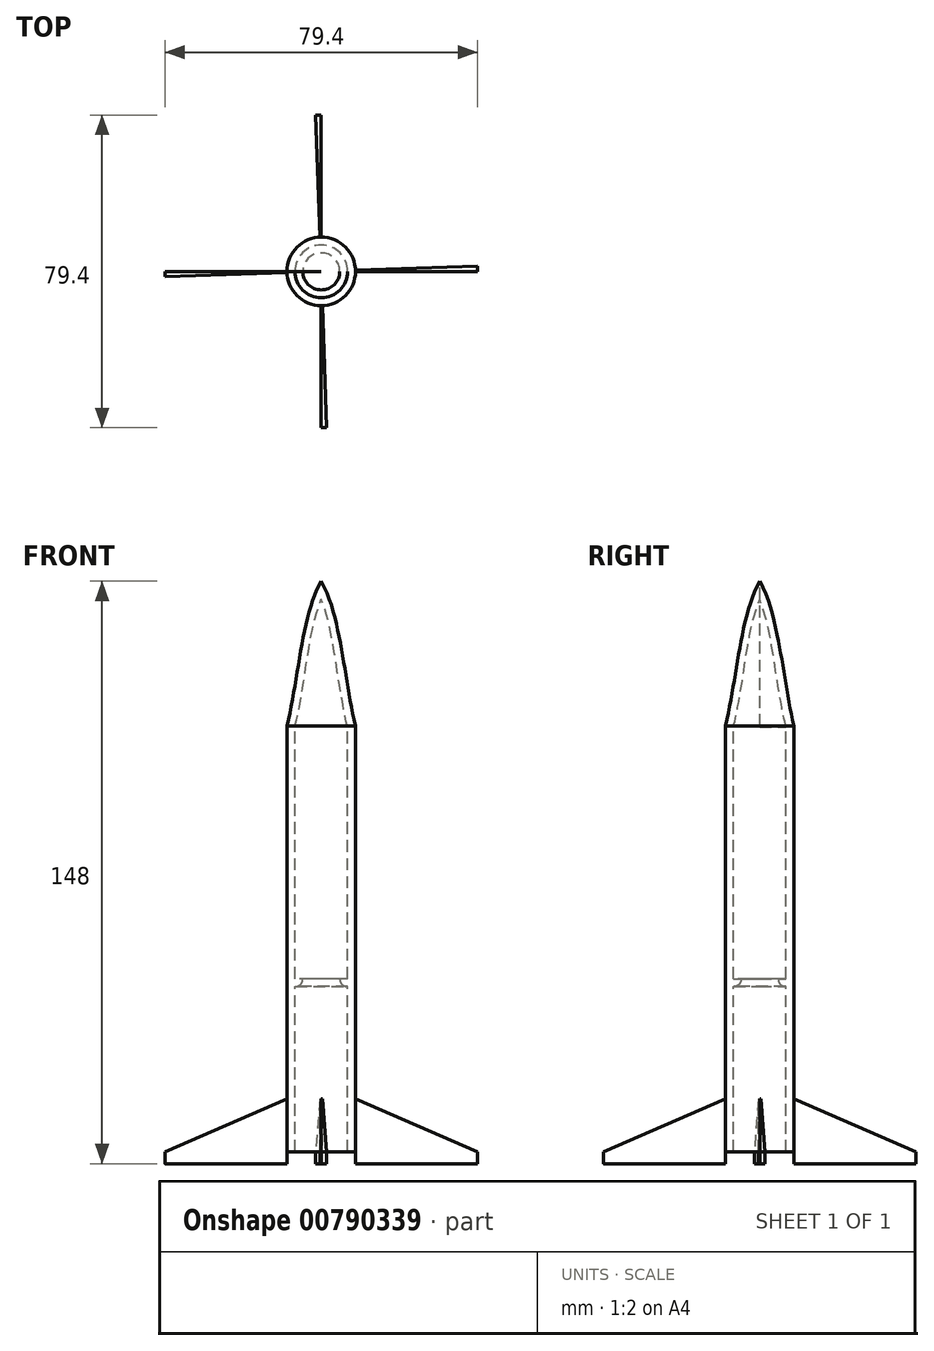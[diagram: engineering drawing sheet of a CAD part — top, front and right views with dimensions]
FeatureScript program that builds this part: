
annotation { "Feature Type Name" : "Feature", "Feature Type Description" : "" }
export const myFeature = defineFeature(function(context is Context, id is Id, definition is map)
    precondition{}
    {
        {
            var Q0;
            Q0=qCreatedBy(makeId("Front.planeOp"),FACE);
            var sketch = newSketch(context, id + "F0", { "sketchPlane" : qUnion([Q0])});
            skLineSegment(sketch, "E0", {"start": v(0, 145) * mm, "end": v(0, 143) * mm});
            skLineSegment(sketch, "E1", {"start": v(0, 143) * mm, "end": v(-13.5, 143) * mm, "construction": true});
            skLineSegment(sketch, "E2", {"start": v(-6.7, 108) * mm, "end": v(-6.7, 0) * mm});
            skLineSegment(sketch, "E3.1", {"start": v(-8.7, 108.2) * mm, "end": v(-8.7, 0) * mm});
            skLineSegment(sketch, "E4", {"start": v(-8.7, 0) * mm, "end": v(-6.7, 0) * mm});
            skLineSegment(sketch, "E5", {"start": v(-6.7, 0) * mm, "end": v(-6.7, 42) * mm});
            skLineSegment(sketch, "E6", {"start": v(-6.7, 42) * mm, "end": v(-4.7, 42) * mm});
            skLineSegment(sketch, "E7", {"start": v(-4.7, 42) * mm, "end": v(-4.7, 44) * mm});
            skLineSegment(sketch, "E8", {"start": v(-4.7, 44) * mm, "end": v(-6.7, 44) * mm});
            skLineSegment(sketch, "E9", {"start": v(0, 145) * mm, "end": v(0, 0) * mm});
            skLineSegment(sketch, "E10", {"start": v(-6.7, 108) * mm, "end": v(0, 108) * mm, "construction": true});
            skLineSegment(sketch, "E11", {"start": v(-8.7, 108.2) * mm, "end": v(0, 108) * mm, "construction": true});
            skLineSegment(sketch, "E12", {"start": v(0, 143) * mm, "end": v(0, 136.34) * mm, "construction": true});
            skFitSpline(sketch, "E13", {"points": [v(-8.7, 108.2) * mm, v(0, 145) * mm], "startDerivative": vector(8.7, 36.8) * mm, "endDerivative": vector(14.37, 24.57) * mm});
            skLineSegment(sketch, "E14", {"start": v(0, 145) * mm, "end": v(0, 136.34) * mm});
            skFitSpline(sketch, "E15.0", {"points": [v(-6.75, 107.75) * mm, v(-6, 110.89) * mm, v(-4.78, 117.6) * mm, v(-3.15, 127.92) * mm, v(-1.5, 135.77) * mm, v(0.2, 140.96) * mm, v(1.2, 143.08) * mm, v(1.73, 144) * mm]});
            skSolve(sketch);
        }
        {
            var Q0;
            {var subQ0=sQuery(id+"F0.wireOp",EDGE,"E3.1");Q0=makeQuery(id+"F0.imprint","IMPRINT",FACE,{"disambiguationData":[TD([[makeQuery(id+"F0.imprint","IMPRINT",EDGE,{"derivedFrom":subQ0}),1.0]])]});}
            var Q1;
            {var subQ0=sQuery(id+"F0.wireOp",EDGE,"E6");Q1=makeQuery(id+"F0.imprint","IMPRINT",FACE,{"disambiguationData":[TD([[makeQuery(id+"F0.imprint","IMPRINT",EDGE,{"derivedFrom":subQ0}),1.0]])]});}
            var Q2;
            {var subQ0=sQuery(id+"F0.wireOp",EDGE,"E9");var subQ1=sQuery(id+"F0.wireOp",EDGE,"E1");var subQ2=makeQuery(id+"F0.imprint","INTERSECT",VERTEX,{"derivedFrom":[subQ1,subQ0]});Q2=makeQuery(id+"F0.imprint","IMPRINT",FACE,{"disambiguationData":[TD([[makeQuery(id+"F0.imprint","IMPRINT",EDGE,{"disambiguationData":[TD([[subQ2,-1.0]])],"derivedFrom":subQ1}),-1.0]])]});}
            var Q3;
            Q3=sQuery(id+"F0.wireOp",EDGE,"E9");
            revolve(context, id + "F1", {"surfaceOperationType" : NewSurfaceOperationType.NEW, "entities" : qUnion([Q0, Q1, Q2]), "axis" : qUnion([Q3]), "revolveType" : RevolveType.FULL});
        }
        {
            var Q0;
            Q0=qCreatedBy(makeId("Right.planeOp"),FACE);
            var sketch = newSketch(context, id + "F2", { "sketchPlane" : qUnion([Q0])});
            skLineSegment(sketch, "E16", {"start": v(8.7, -3) * mm, "end": v(39.7, -3) * mm});
            skLineSegment(sketch, "E17", {"start": v(39.7, -3) * mm, "end": v(39.7, 0) * mm});
            skLineSegment(sketch, "E18", {"start": v(8.7, 0) * mm, "end": v(8.7, 13.5) * mm});
            skLineSegment(sketch, "E19", {"start": v(8.7, 13.5) * mm, "end": v(39.7, 0) * mm});
            skLineSegment(sketch, "E20", {"start": v(8.7, -3) * mm, "end": v(8.7, 0) * mm});
            skLineSegment(sketch, "E21", {"start": v(0, 0) * mm, "end": v(0, 51.2) * mm});
            skLineSegment(sketch, "E22", {"start": v(8.7, 0) * mm, "end": v(0, 0) * mm, "construction": true});
            skLineSegment(sketch, "E23", {"start": v(8.7, 13.5) * mm, "end": v(8.7, -3) * mm});
            skSolve(sketch);
        }
        {
            var Q0;
            Q0=makeQuery(id+"F2.imprint","IMPRINT",FACE,{"disambiguationData":[TD([[makeQuery(id+"F2.imprint","IMPRINT",EDGE,{"derivedFrom":sQuery(id+"F2.wireOp",EDGE,"E16")}),1.0]])]});
            var Q1;
            Q1=sQuery(id+"F2.wireOp",EDGE,"E21");
            revolve(context, id + "F3", {"surfaceOperationType" : NewSurfaceOperationType.NEW, "entities" : qUnion([Q0]), "axis" : qUnion([Q1]), "revolveType" : RevolveType.ONE_DIRECTION, "angle" : 2 * degree});
        }
        {
            var Q0;
            Q0=makeQuery(id+"F3.opRevolve","SWEPT_BODY",BODY,{"disambiguationData":[OSD([sQuery(id+"F2.wireOp",EDGE,"E16"),sQuery(id+"F2.wireOp",EDGE,"E17"),sQuery(id+"F2.wireOp",EDGE,"E18"),sQuery(id+"F2.wireOp",EDGE,"E19"),sQuery(id+"F2.wireOp",EDGE,"E20")])]});
            var Q1;
            Q1=sQuery(id+"F2.wireOp",EDGE,"E21");
            circularPattern(context, id + "F4", {"entities" : qUnion([Q0]), "axis" : qUnion([Q1]), "angle" : 360 * degree, "instanceCount" : 4, "equalSpace" : true});
        }
        {
            var Q0;
            Q0=makeQuery(id+"F1.opRevolve","SWEPT_EDGE",EDGE,{"disambiguationData":[OSD([sQuery(id+"F0.wireOp",EDGE,"E6"),sQuery(id+"F0.wireOp",EDGE,"E7")])]});
            fillet(context, id + "F5", {"entities" : qUnion([Q0]), "radius" : 1.9 * mm, "tangentPropagation" : true, "allowEdgeOverflow" : false});
        }
    });
